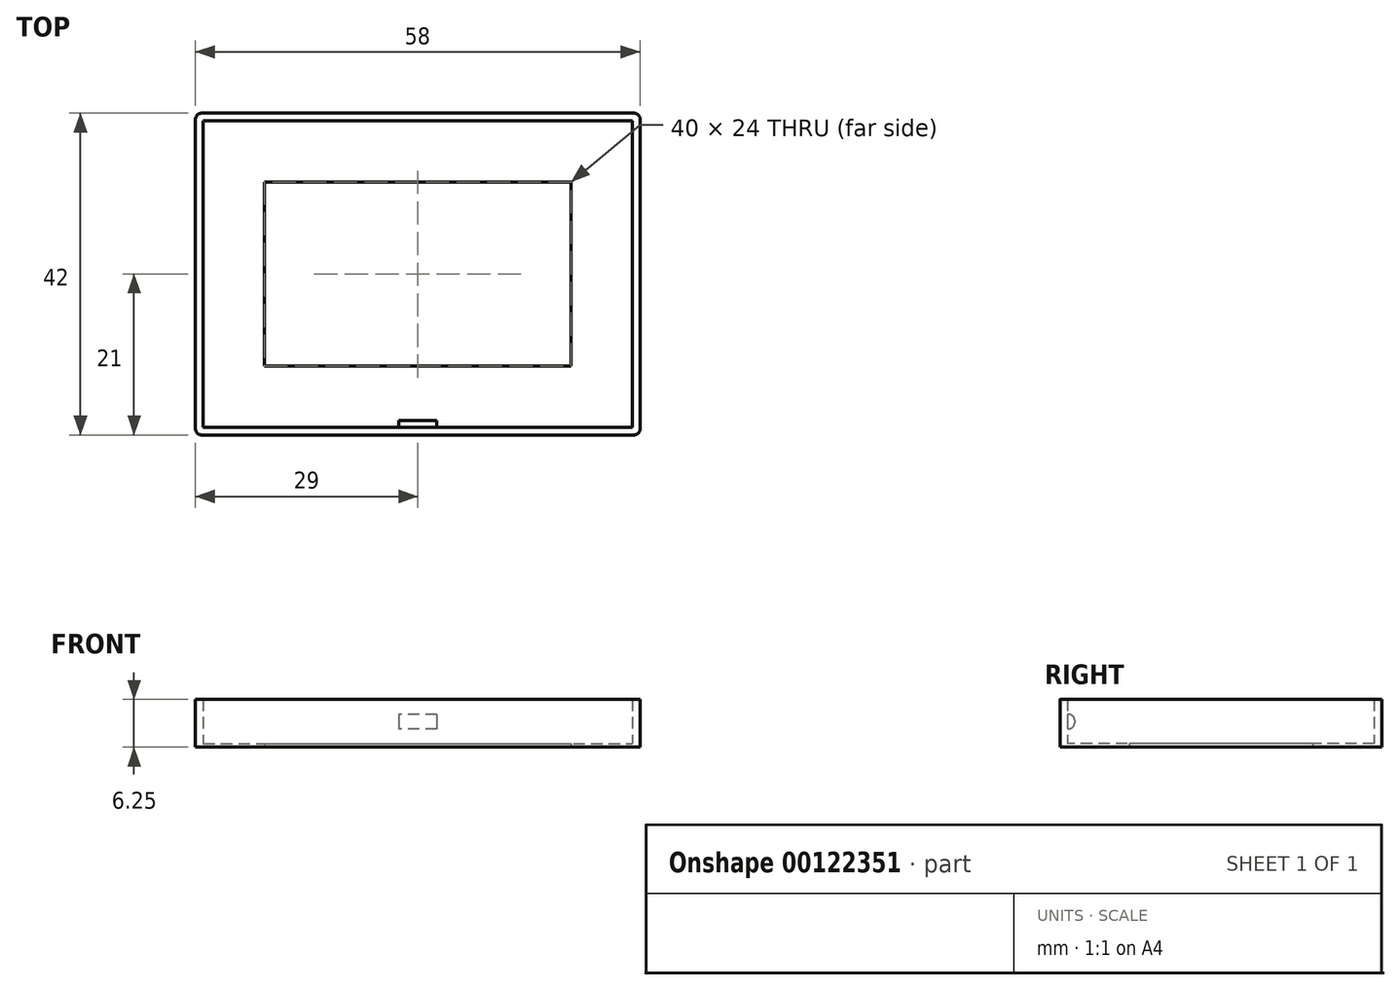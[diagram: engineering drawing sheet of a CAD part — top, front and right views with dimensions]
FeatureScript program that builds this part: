
annotation { "Feature Type Name" : "Feature", "Feature Type Description" : "" }
export const myFeature = defineFeature(function(context is Context, id is Id, definition is map)
    precondition{}
    {
        {
            var Q0;
            Q0=qCreatedBy(makeId("Top.planeOp"),FACE);
            var sketch = newSketch(context, id + "F0", { "sketchPlane" : qUnion([Q0])});
            skLineSegment(sketch, "E0.bottom", {"start": v(-28, 20) * mm, "end": v(28, 20) * mm});
            skLineSegment(sketch, "E0.top", {"start": v(-28, -20) * mm, "end": v(28, -20) * mm});
            skLineSegment(sketch, "E0.left", {"start": v(-28, 20) * mm, "end": v(-28, -20) * mm});
            skLineSegment(sketch, "E0.right", {"start": v(28, 20) * mm, "end": v(28, -20) * mm});
            skLineSegment(sketch, "E1.0", {"start": v(-29, 21) * mm, "end": v(-29, -21) * mm});
            skLineSegment(sketch, "E1.1", {"start": v(-29, 21) * mm, "end": v(29, 21) * mm});
            skLineSegment(sketch, "E1.2", {"start": v(29, 21) * mm, "end": v(29, -21) * mm});
            skLineSegment(sketch, "E1.3", {"start": v(-29, -21) * mm, "end": v(29, -21) * mm});
            skLineSegment(sketch, "E2.0", {"start": v(-20, 12) * mm, "end": v(-20, -12) * mm});
            skLineSegment(sketch, "E2.1", {"start": v(-20, 12) * mm, "end": v(20, 12) * mm});
            skLineSegment(sketch, "E2.2", {"start": v(20, 12) * mm, "end": v(20, -12) * mm});
            skLineSegment(sketch, "E2.3", {"start": v(-20, -12) * mm, "end": v(20, -12) * mm});
            skSolve(sketch);
        }
        {
            var Q0;
            Q0=makeQuery(id+"F0.imprint","IMPRINT",FACE,{"disambiguationData":[TD([[makeQuery(id+"F0.imprint","IMPRINT",EDGE,{"derivedFrom":sQuery(id+"F0.wireOp",EDGE,"E0.bottom")}),-1.0]])]});
            extrude(context, id + "F1", {"entities" : qUnion([Q0]), "depth" : 0.5 * mm});
        }
        {
            var Q0;
            Q0=makeQuery(id+"F0.imprint","IMPRINT",FACE,{"disambiguationData":[TD([[makeQuery(id+"F0.imprint","IMPRINT",EDGE,{"derivedFrom":sQuery(id+"F0.wireOp",EDGE,"E0.bottom")}),1.0]])]});
            extrude(context, id + "F2", {"entities" : qUnion([Q0]), "operationType" : NewBodyOperationType.ADD, "depth" : 6.25 * mm});
        }
        {
            var Q0;
            Q0=makeQuery(id+"F2.opExtrude","SWEPT_FACE",FACE,{"disambiguationData":[OSD([sQuery(id+"F0.wireOp",EDGE,"E0.top")])]});
            var sketch = newSketch(context, id + "F3", { "sketchPlane" : qUnion([Q0])});
            skLineSegment(sketch, "E3.bottom", {"start": v(-2.5, 4.3) * mm, "end": v(2.5, 4.3) * mm});
            skLineSegment(sketch, "E3.top", {"start": v(-2.5, 2.4) * mm, "end": v(2.5, 2.4) * mm});
            skLineSegment(sketch, "E3.left", {"start": v(-2.5, 4.3) * mm, "end": v(-2.5, 2.4) * mm});
            skLineSegment(sketch, "E3.right", {"start": v(2.5, 4.3) * mm, "end": v(2.5, 2.4) * mm});
            skSolve(sketch);
        }
        {
            var Q0;
            Q0=makeQuery(id+"F3.imprint","IMPRINT",FACE,{"disambiguationData":[TD([[makeQuery(id+"F3.imprint","IMPRINT",EDGE,{"derivedFrom":sQuery(id+"F3.wireOp",EDGE,"E3.bottom")}),-1.0]])]});
            extrude(context, id + "F4", {"entities" : qUnion([Q0]), "operationType" : NewBodyOperationType.ADD, "depth" : 0.9 * mm});
        }
        {
            var Q0;
            Q0=makeQuery(id+"F4.opExtrude","CAP_EDGE",EDGE,{"disambiguationData":[OSD([sQuery(id+"F3.wireOp",EDGE,"E3.bottom")])],"isStart":false});
            var Q1;
            Q1=makeQuery(id+"F4.opExtrude","CAP_EDGE",EDGE,{"disambiguationData":[OSD([sQuery(id+"F3.wireOp",EDGE,"E3.top")])],"isStart":false});
            var Q2;
            Q2=makeQuery(id+"FQwNc8HySaX4Y21_1.1.F4.opExtrude","CAP_EDGE",EDGE,{"disambiguationData":[OSD([sQuery(id+"F3.wireOp",EDGE,"E3.bottom")])],"isStart":false});
            var Q3;
            Q3=makeQuery(id+"FQwNc8HySaX4Y21_1.1.F4.opExtrude","CAP_EDGE",EDGE,{"disambiguationData":[OSD([sQuery(id+"F3.wireOp",EDGE,"E3.top")])],"isStart":false});
            fillet(context, id + "F5", {"entities" : qUnion([Q0, Q1, Q2, Q3]), "radius" : 0.8 * mm, "tangentPropagation" : true, "allowEdgeOverflow" : false});
        }
        {
            var Q0;
            Q0=makeQuery(id+"F2.opExtrude","SWEPT_EDGE",EDGE,{"disambiguationData":[OSD([sQuery(id+"F0.wireOp",EDGE,"E1.0"),sQuery(id+"F0.wireOp",EDGE,"E1.1")])]});
            var Q1;
            Q1=makeQuery(id+"F2.opExtrude","SWEPT_EDGE",EDGE,{"disambiguationData":[OSD([sQuery(id+"F0.wireOp",EDGE,"E1.0"),sQuery(id+"F0.wireOp",EDGE,"E1.3")])]});
            var Q2;
            Q2=makeQuery(id+"F2.opExtrude","SWEPT_EDGE",EDGE,{"disambiguationData":[OSD([sQuery(id+"F0.wireOp",EDGE,"E1.1"),sQuery(id+"F0.wireOp",EDGE,"E1.2")])]});
            var Q3;
            Q3=makeQuery(id+"F2.opExtrude","SWEPT_EDGE",EDGE,{"disambiguationData":[OSD([sQuery(id+"F0.wireOp",EDGE,"E1.2"),sQuery(id+"F0.wireOp",EDGE,"E1.3")])]});
            fillet(context, id + "F6", {"entities" : qUnion([Q0, Q1, Q2, Q3]), "radius" : 0.8 * mm, "tangentPropagation" : true, "allowEdgeOverflow" : false});
        }
    });
